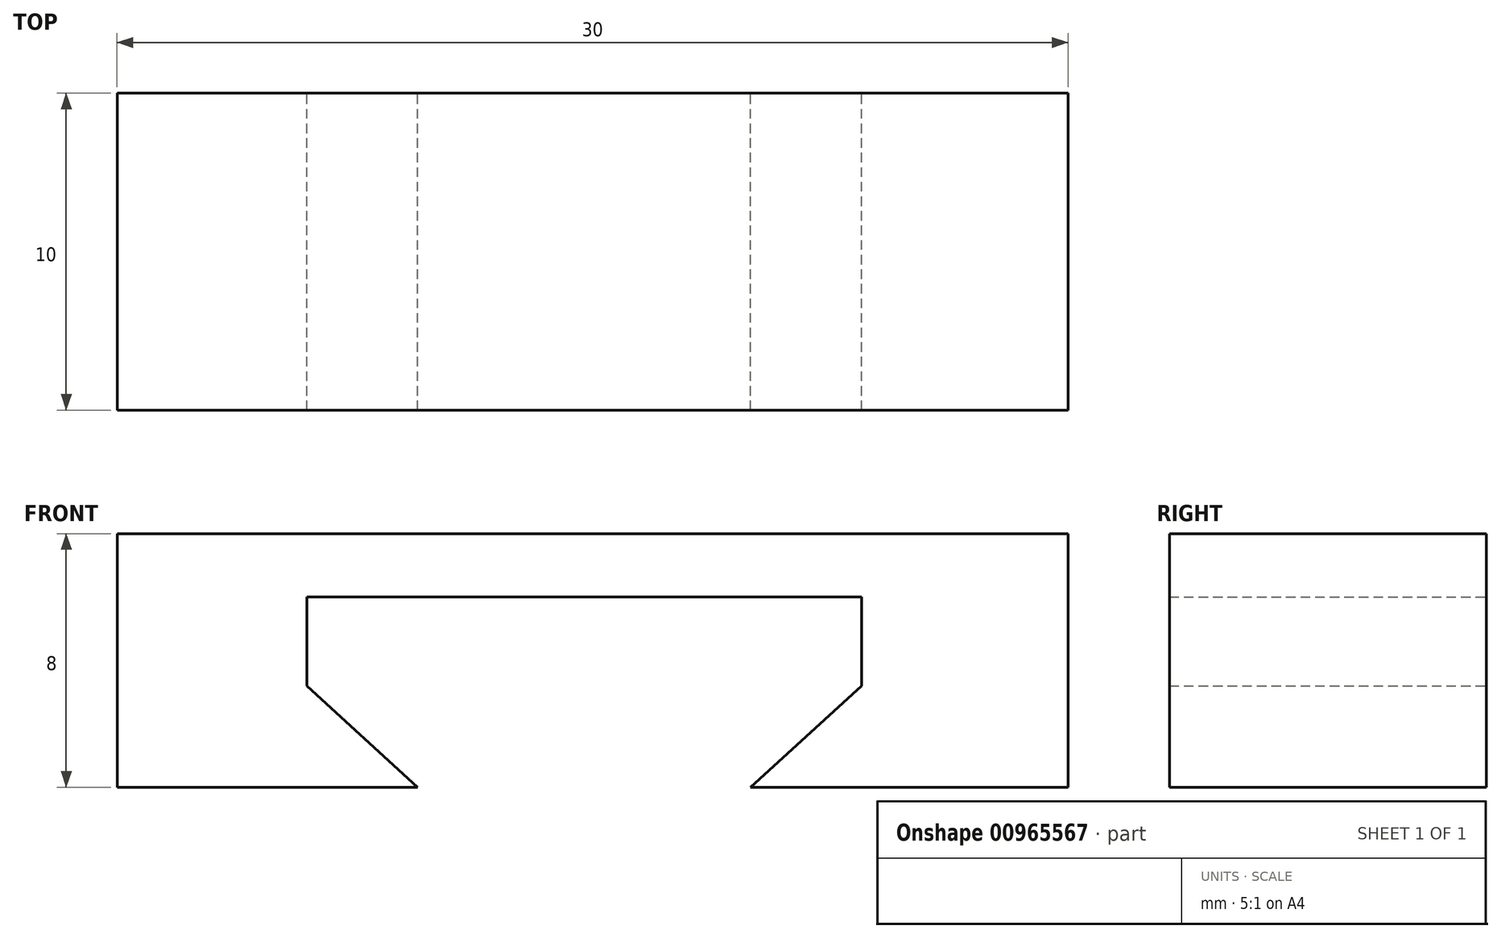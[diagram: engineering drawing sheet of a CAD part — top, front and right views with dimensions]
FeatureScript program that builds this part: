
annotation { "Feature Type Name" : "Feature", "Feature Type Description" : "" }
export const myFeature = defineFeature(function(context is Context, id is Id, definition is map)
    precondition{}
    {
        {
            var Q0;
            Q0=qCreatedBy(makeId("Front.planeOp"),FACE);
            var sketch = newSketch(context, id + "F0", { "sketchPlane" : qUnion([Q0])});
            skLineSegment(sketch, "E0.top", {"start": v(-14.56, -9.67) * mm, "end": v(15.44, -9.67) * mm});
            skLineSegment(sketch, "E0.left", {"start": v(-14.56, -1.67) * mm, "end": v(-14.56, -9.67) * mm});
            skLineSegment(sketch, "E0.right", {"start": v(15.44, -1.67) * mm, "end": v(15.44, -9.67) * mm});
            skLineSegment(sketch, "E1.bottom", {"start": v(-8.57, -3.67) * mm, "end": v(8.93, -3.67) * mm});
            skLineSegment(sketch, "E1.top", {"start": v(-8.57, -9.67) * mm, "end": v(8.93, -9.67) * mm});
            skLineSegment(sketch, "E1.left", {"start": v(-8.57, -3.67) * mm, "end": v(-8.57, -9.67) * mm});
            skLineSegment(sketch, "E1.right", {"start": v(8.93, -3.67) * mm, "end": v(8.93, -9.67) * mm});
            skLineSegment(sketch, "E2.left", {"start": v(-8.57, -9.67) * mm, "end": v(-8.57, -5.78) * mm});
            skLineSegment(sketch, "E3.left", {"start": v(8.93, -9.67) * mm, "end": v(8.93, -5.67) * mm});
            skPoint(sketch, "E4", {"position": v(-8.57, -6.67) * mm});
            skLineSegment(sketch, "E5.bottom", {"start": v(-8.57, -9.67) * mm, "end": v(-9.71, -9.67) * mm, "construction": true});
            skLineSegment(sketch, "E5.top", {"start": v(-8.57, -6.47) * mm, "end": v(-9.71, -6.47) * mm, "construction": true});
            skLineSegment(sketch, "E5.left", {"start": v(-8.57, -9.67) * mm, "end": v(-8.57, -6.47) * mm, "construction": true});
            skLineSegment(sketch, "E5.right", {"start": v(-9.71, -9.67) * mm, "end": v(-9.71, -6.47) * mm, "construction": true});
            skPoint(sketch, "E6.oppositeSnap0", {"position": v(-9.14, -6.47) * mm});
            skLineSegment(sketch, "E6.bottom", {"start": v(8.93, -9.67) * mm, "end": v(10.57, -9.67) * mm, "construction": true});
            skLineSegment(sketch, "E6.top", {"start": v(8.93, -6.47) * mm, "end": v(10.57, -6.47) * mm, "construction": true});
            skLineSegment(sketch, "E6.left", {"start": v(8.93, -9.67) * mm, "end": v(8.93, -6.47) * mm, "construction": true});
            skLineSegment(sketch, "E6.right", {"start": v(10.57, -9.67) * mm, "end": v(10.57, -6.47) * mm, "construction": true});
            skLineSegment(sketch, "E7.bottom", {"start": v(-8.57, -9.67) * mm, "end": v(-5.07, -9.67) * mm, "construction": true});
            skLineSegment(sketch, "E7.top", {"start": v(-8.57, -11.6) * mm, "end": v(-5.07, -11.6) * mm, "construction": true});
            skLineSegment(sketch, "E7.left", {"start": v(-8.57, -9.67) * mm, "end": v(-8.57, -11.6) * mm, "construction": true});
            skLineSegment(sketch, "E7.right", {"start": v(-5.07, -9.67) * mm, "end": v(-5.07, -11.6) * mm, "construction": true});
            skLineSegment(sketch, "E8.bottom", {"start": v(8.93, -9.67) * mm, "end": v(5.43, -9.67) * mm, "construction": true});
            skLineSegment(sketch, "E8.top", {"start": v(8.93, -11.48) * mm, "end": v(5.43, -11.48) * mm, "construction": true});
            skLineSegment(sketch, "E8.left", {"start": v(8.93, -9.67) * mm, "end": v(8.93, -11.48) * mm, "construction": true});
            skLineSegment(sketch, "E8.right", {"start": v(5.43, -9.67) * mm, "end": v(5.43, -11.48) * mm, "construction": true});
            skLineSegment(sketch, "E9", {"start": v(-8.57, -6.47) * mm, "end": v(-5.07, -9.67) * mm});
            skLineSegment(sketch, "E10", {"start": v(5.43, -9.67) * mm, "end": v(8.93, -6.47) * mm});
            skLineSegment(sketch, "E11", {"start": v(-14.56, -1.67) * mm, "end": v(15.44, -1.67) * mm});
            skSolve(sketch);
        }
        {
            var Q0;
            {var subQ7=sQuery(id+"F0.wireOp",EDGE,"E0.left");Q0=makeQuery(id+"F0.imprint","IMPRINT",FACE,{"disambiguationData":[TD([[makeQuery(id+"F0.imprint","IMPRINT",EDGE,{"derivedFrom":subQ7}),1.0]])]});}
            var Q1;
            {var subQ3=sQuery(id+"F0.wireOp",EDGE,"E9");Q1=makeQuery(id+"F0.imprint","IMPRINT",FACE,{"disambiguationData":[TD([[makeQuery(id+"F0.imprint","IMPRINT",EDGE,{"derivedFrom":subQ3}),-1.0]])]});}
            var Q2;
            {var subQ3=sQuery(id+"F0.wireOp",EDGE,"E10");Q2=makeQuery(id+"F0.imprint","IMPRINT",FACE,{"disambiguationData":[TD([[makeQuery(id+"F0.imprint","IMPRINT",EDGE,{"derivedFrom":subQ3}),-1.0]])]});}
            extrude(context, id + "F1", {"entities" : qUnion([Q0, Q1, Q2]), "depth" : 10 * mm, "offsetDistance" : 25 * mm});
        }
    });
